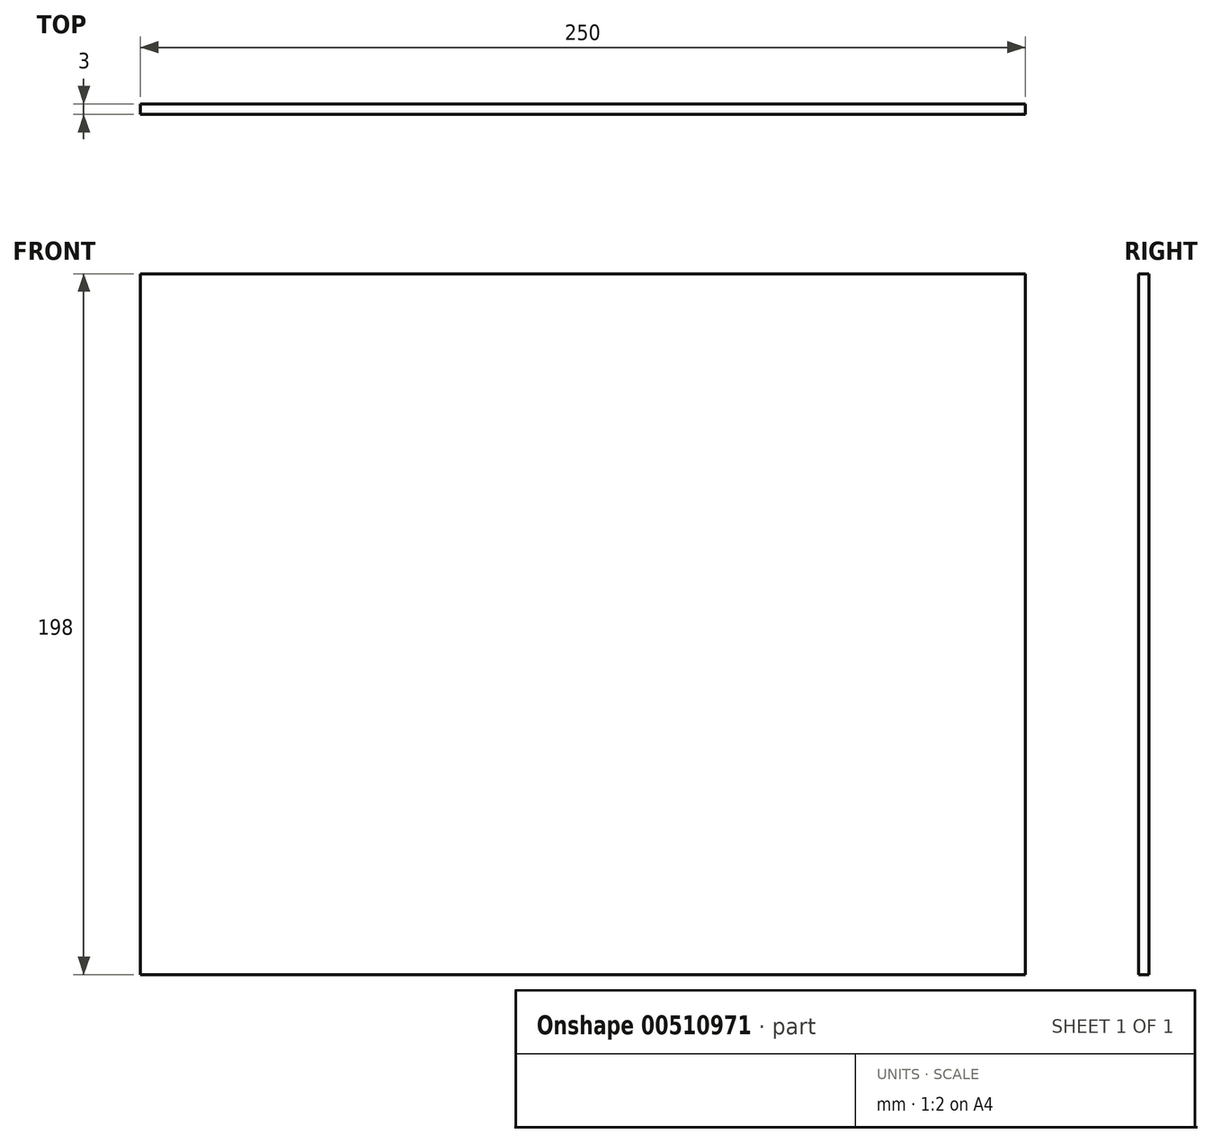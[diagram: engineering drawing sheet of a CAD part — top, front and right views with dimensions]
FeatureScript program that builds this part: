
annotation { "Feature Type Name" : "Feature", "Feature Type Description" : "" }
export const myFeature = defineFeature(function(context is Context, id is Id, definition is map)
    precondition{}
    {
        {
            var Q0;
            Q0=qCreatedBy(makeId("Front.planeOp"),FACE);
            var sketch = newSketch(context, id + "F0", { "sketchPlane" : qUnion([Q0])});
            skLineSegment(sketch, "E0.bottom", {"start": v(-125, 99) * mm, "end": v(125, 99) * mm});
            skLineSegment(sketch, "E0.top", {"start": v(-125, -99) * mm, "end": v(125, -99) * mm});
            skLineSegment(sketch, "E0.left", {"start": v(-125, 99) * mm, "end": v(-125, -99) * mm});
            skLineSegment(sketch, "E0.right", {"start": v(125, 99) * mm, "end": v(125, -99) * mm});
            skPoint(sketch, "E0.middle", {"position": v(0, 0) * mm});
            skSolve(sketch);
        }
        {
            var Q0;
            Q0=makeQuery(id+"F0.imprint","IMPRINT",FACE,{"disambiguationData":[TD([[makeQuery(id+"F0.imprint","IMPRINT",EDGE,{"derivedFrom":sQuery(id+"F0.wireOp",EDGE,"E0.bottom")}),-1.0]])]});
            extrude(context, id + "F1", {"entities" : qUnion([Q0]), "depth" : 3 * mm, "offsetDistance" : 25 * mm});
        }
    });
